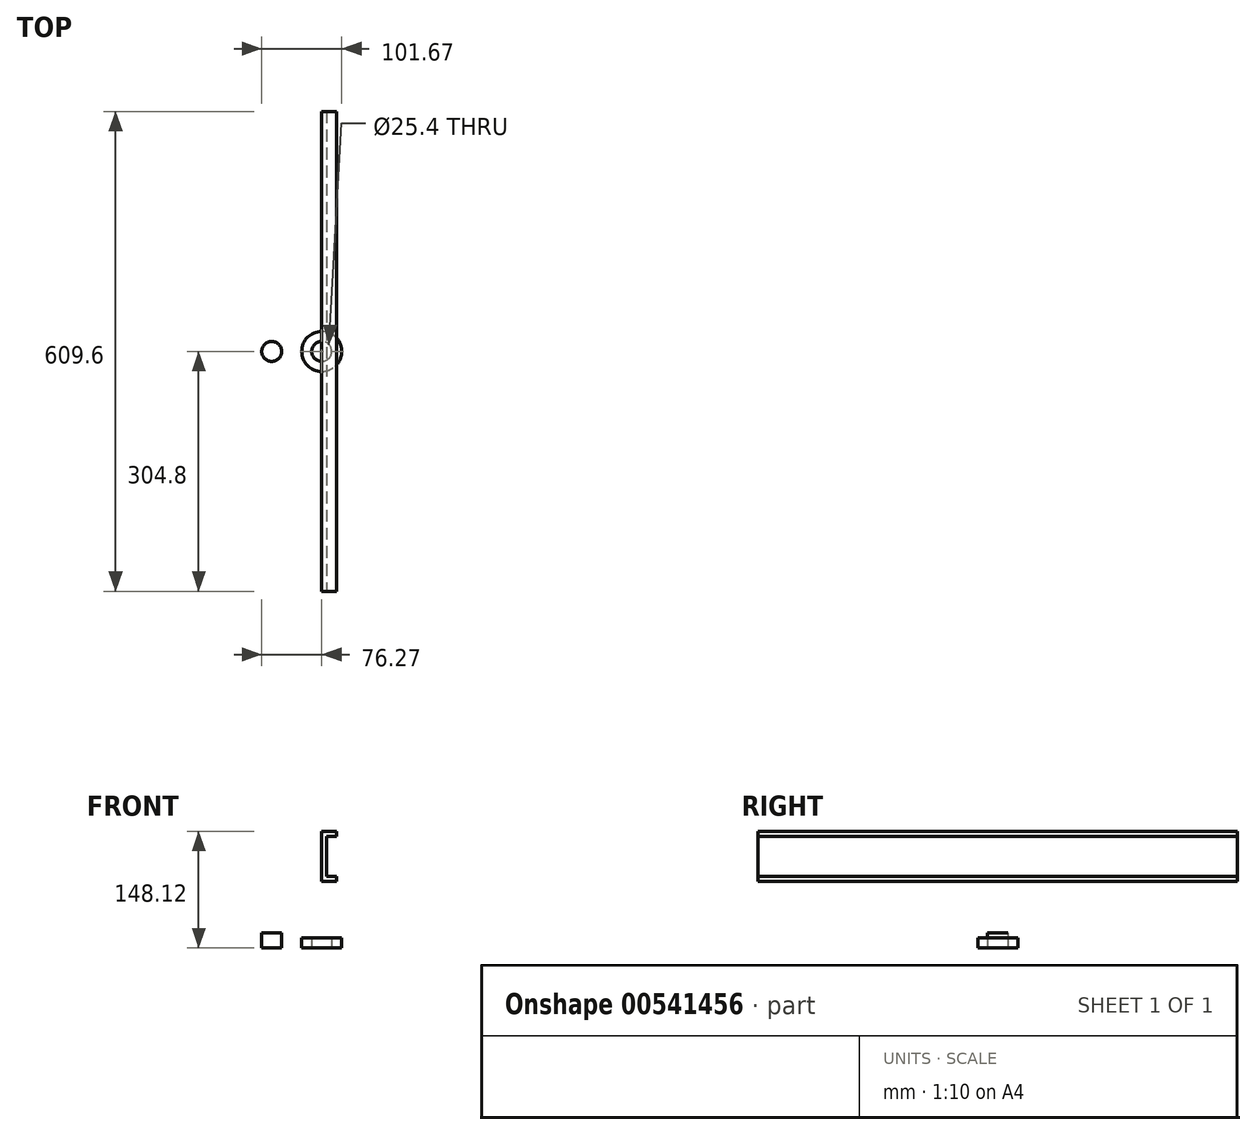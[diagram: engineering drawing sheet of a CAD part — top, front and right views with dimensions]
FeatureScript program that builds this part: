
annotation { "Feature Type Name" : "Feature", "Feature Type Description" : "" }
export const myFeature = defineFeature(function(context is Context, id is Id, definition is map)
    precondition{}
    {
        {
            var Q0;
            Q0=qCreatedBy(makeId("Top.planeOp"),FACE);
            var sketch = newSketch(context, id + "F0", { "sketchPlane" : qUnion([Q0])});
            skCircle(sketch, "E0", {"center": v(0, 0) * mm, "radius": 12.7 * mm});
            skCircle(sketch, "E1", {"center": v(0, 0) * mm, "radius": 25.4 * mm});
            skSolve(sketch);
        }
        {
            var Q0;
            Q0=makeQuery(id+"F0.imprint","IMPRINT",FACE,{"disambiguationData":[TD([[makeQuery(id+"F0.imprint","IMPRINT",EDGE,{"derivedFrom":sQuery(id+"F0.wireOp",EDGE,"E0")}),-1.0]])]});
            extrude(context, id + "F1", {"entities" : qUnion([Q0]), "depth" : 12.7 * mm, "offsetDistance" : 25.4 * mm});
        }
        {
            var Q0;
            Q0=qCreatedBy(makeId("Top.planeOp"),FACE);
            var sketch = newSketch(context, id + "F2", { "sketchPlane" : qUnion([Q0])});
            skCircle(sketch, "E2", {"center": v(-63.57, 0) * mm, "radius": 12.7 * mm});
            skSolve(sketch);
        }
        {
            var Q0;
            Q0=makeQuery(id+"F2.imprint","IMPRINT",FACE,{"disambiguationData":[TD([[makeQuery(id+"F2.imprint","IMPRINT",EDGE,{"derivedFrom":sQuery(id+"F2.wireOp",EDGE,"E2")}),1.0]])]});
            extrude(context, id + "F3", {"entities" : qUnion([Q0]), "depth" : 19.05 * mm, "offsetDistance" : 25.4 * mm});
        }
        {
            var Q0;
            Q0=qCreatedBy(makeId("Right.planeOp"),FACE);
            var sketch = newSketch(context, id + "F4", { "sketchPlane" : qUnion([Q0])});
            skLineSegment(sketch, "E3.bottom", {"start": v(-304.8, 148.12) * mm, "end": v(304.8, 148.12) * mm});
            skLineSegment(sketch, "E3.top", {"start": v(-304.8, 84.62) * mm, "end": v(304.8, 84.62) * mm});
            skLineSegment(sketch, "E3.left", {"start": v(-304.8, 148.12) * mm, "end": v(-304.8, 84.62) * mm});
            skLineSegment(sketch, "E3.right", {"start": v(304.8, 148.12) * mm, "end": v(304.8, 84.62) * mm});
            skPoint(sketch, "E3.middle", {"position": v(0, 116.37) * mm});
            skSolve(sketch);
        }
        {
            var Q0;
            Q0=makeQuery(id+"F4.imprint","IMPRINT",FACE,{"disambiguationData":[TD([[makeQuery(id+"F4.imprint","IMPRINT",EDGE,{"derivedFrom":sQuery(id+"F4.wireOp",EDGE,"E3.bottom")}),-1.0]])]});
            extrude(context, id + "F5", {"entities" : qUnion([Q0]), "depth" : 19.05 * mm, "offsetDistance" : 25.4 * mm});
        }
        {
            var Q0;
            Q0=makeQuery(id+"F5.opExtrude","CAP_FACE",FACE,{"disambiguationData":[OSD([sQuery(id+"F4.wireOp",EDGE,"E3.bottom"),sQuery(id+"F4.wireOp",EDGE,"E3.top"),sQuery(id+"F4.wireOp",EDGE,"E3.left"),sQuery(id+"F4.wireOp",EDGE,"E3.right")])],"isStart":false});
            var sketch = newSketch(context, id + "F6", { "sketchPlane" : qUnion([Q0])});
            skLineSegment(sketch, "E4", {"start": v(304.8, 141.77) * mm, "end": v(-304.8, 141.77) * mm});
            skLineSegment(sketch, "E5", {"start": v(304.8, 90.97) * mm, "end": v(-304.8, 90.97) * mm});
            skSolve(sketch);
        }
        {
            var Q0;
            Q0 = qSketchRegion(id + "F6", true);
            var Q1;
            {var subQ0=sQuery(id+"F6.wireOp",EDGE,"E4");Q1=makeQuery(id+"F6.imprint","IMPRINT",FACE,{"disambiguationData":[TD([[makeQuery(id+"F6.imprint","IMPRINT",EDGE,{"derivedFrom":subQ0}),1.0]])]});}
            extrude(context, id + "F7", {"entities" : qUnion([Q0, Q1]), "operationType" : NewBodyOperationType.REMOVE, "oppositeDirection" : true, "depth" : 12.7 * mm, "offsetDistance" : 25.4 * mm});
        }
    });
